# Revit family: Door_Bifold System_2Panel_Solid
name_source: partatom
category: Doors
units: mm (PartAtom-declared; Revit-internal decimal feet)

## family parameters
Always vertical = Yes
Cut with Voids When Loaded = No
Host = Wall
OmniClass Number = 23.30.10.11.14
OmniClass Title = Door
Room Calculation Point = No
Shared = Yes

## types (1)
- 1980h x 810w x 40t
    Analytic Construction = Solid core wood
    ClearanceLeft = 100 mm  [stored 0.328084 ft]
    ClearanceRight = 100 mm  [stored 0.328084 ft]
    Description = Nz - Bifold Glazed
    Fire Rating = 30/30/30
    FrameByThroat = Yes
    FrameDepth = 150 mm  [stored 0.492126 ft]
    FrameOffsetExt = 0 mm  [stored 0 ft]
    FrameOffsetExtControl = 0 mm  [stored 0 ft]
    FrameOffsetInt = 0 mm  [stored 0 ft]
    FrameOffsetIntControl = 0 mm  [stored 0 ft]
    Function = Exterior
    HandleHeight = 1000 mm  [stored 3.28084 ft]
    HandleInset = 50 mm  [stored 0.164042 ft]
    HeadHeight = 40 mm  [stored 0.131234 ft]
    HeadTolerance = 0 mm  [stored 0 ft]
    Heat Transfer Coefficient (U) = 2.6119 W/(m²·K)
    Height = 1980 mm  [stored 6.49606 ft]
    JambTolerance = 0 mm  [stored 0 ft]
    JambWidth = 40 mm  [stored 0.131234 ft]
    LeafHeight = 1980 mm  [stored 6.49606 ft]
    LeafInsetDist = 0 mm  [stored 0 ft]
    LeafWidth1 = 405 mm  [stored 1.32874 ft]
    Manufacturer = Generic
    Solar Heat Gain Coefficient = 0
    StopDepth = 40 mm  [stored 0.131234 ft]
    StopWidth = 10 mm  [stored 0.0328084 ft]
    Thermal Resistance (R) = 0.3829 (m²·K)/W
    Thickness = 40 mm  [stored 0.131234 ft]
    TrimThickness = 20 mm  [stored 0.0656168 ft]
    TrimWidth = 40 mm  [stored 0.131234 ft]
    TrimWidthControl = 40 mm  [stored 0.131234 ft]
    Type Comments = 1980h x 810w x 40t
    Undercut = 10 mm  [stored 0.0328084 ft]
    Visual Light Transmittance = 0
    Wall Closure = By host
    Website = www.bifoldsystems.co.nz
    Width = 810 mm  [stored 2.65748 ft]

note: [stored X ft] marks values corroborated as IEEE doubles in the binary element streams (Revit-internal decimal feet)

## geometry (parser evidence)
native form markers: Sweep x15
no freeform markers — native parametric forms only
